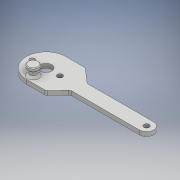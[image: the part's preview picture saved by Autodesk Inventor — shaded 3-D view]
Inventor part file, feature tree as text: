
AUTODESK INVENTOR PART (.ipt)
format: ipt  version: 2018.2 (Build 222227000, 227)  size: 207,872 bytes
history: native  units: mm
features: extrude x7, sketch x6, fillet x6, chamfer x5
ambient origin geometry x8: Origin, YZ Plane, XZ Plane, XY Plane, X Axis, Y Axis, Z Axis, Center Point
bodies: Solid1 (feature_tree)
feature tree (24):
  sketch  "Sketch1"  dims[d0=27.94mm d1=3.683mm d2=3.683mm]
  extrude  "Extrusion1"  Depth=27.94mm
  fillet  "Fillet1"  Radius=3.683mm
  extrude  "Extrusion11"  Depth=10.0mm
  extrude  "Extrusion12"  Depth=2.0mm
  fillet  "Fillet3"  Radius=76.2mm
  fillet  "Fillet4"  Radius=20.0mm
  chamfer  "Chamfer1"  Distance=10.0mm
  fillet  "Fillet5"  Radius=3.75mm
  extrude  "Extrusion13"  Depth=10.0mm TaperAngle=0.0deg
  extrude  "Extrusion14"  Depth=5.0mm
  fillet  "Fillet6"  Radius=10.0mm
  extrude  "Extrusion15"  Depth=2.5mm TaperAngle=45.0deg
  chamfer  "Chamfer2"  Distance=5.0mm
  chamfer  "Chamfer3"  Distance=5.0mm
  chamfer  "Chamfer4"  Distance=10.0mm
  chamfer  "Chamfer5"  Distance=8.0mm
  extrude  "Extrusion16"  Depth=10.0mm TaperAngle=0.0deg
  fillet  "Fillet7"  Radius=5.0mm
  sketch  "Sketch9"  dims[d3=10.0mm d5=23.387412mm]
  sketch  "Sketch10"  dims[d6=3.0mm d7=0.0mm d8=2.0mm d19=76.2mm d36=20.0mm]
  sketch  "Sketch11"  dims[d37=10.0mm]
  sketch  "Sketch12"  dims[d38=5.0mm d39=10.0mm d40=0.0mm d41=3.75mm]
  sketch  "Sketch13"  dims[d42=5.0mm d43=10.0mm d44=0.0mm d45=5.0mm d46=10.0mm d47=2.5mm d48=2.0mm d49=45.0deg d50=5.0mm d51=5.0mm d52=10.0mm d53=0.0mm d54=8.0mm d55=10.0mm d56=0.0mm d57=5.0mm d58=7.5mm d59=7.5mm d60=2.0mm d61=0.0mm d62=1.5mm d63=2.0mm d64=45.0deg d65=1.25mm d66=2.0mm d67=45.0deg d68=1.25mm d69=2.0mm d70=45.0deg d71=0.5mm d72=2.0mm d73=45.0deg d74=10.0mm d75=0.0mm d76=5.0mm]
